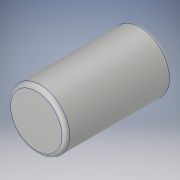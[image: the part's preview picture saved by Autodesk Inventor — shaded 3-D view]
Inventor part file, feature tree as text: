
AUTODESK INVENTOR PART (.ipt)
format: ipt  version: 2018 (Build 220112000, 112)  size: 114,176 bytes
history: native  units: in
note: dims shown in document units (in); Inventor stores cm internally (conversion verified against a paired STEP export)
features: extrude x1, fillet x1, sketch x1
ambient origin geometry x8: Origin, YZ Plane, XZ Plane, XY Plane, X Axis, Y Axis, Z Axis, Center Point
bodies: Solid1 (feature_tree)
feature tree (3):
  extrude  "Extrusion1"  Depth=0.14in TaperAngle=0.0deg
  fillet  "Fillet1"  Radius=0.005in
  sketch  "Sketch1"  dims[d0=0.077in d1=0.14in d2=0.0in d3=0.005in]
